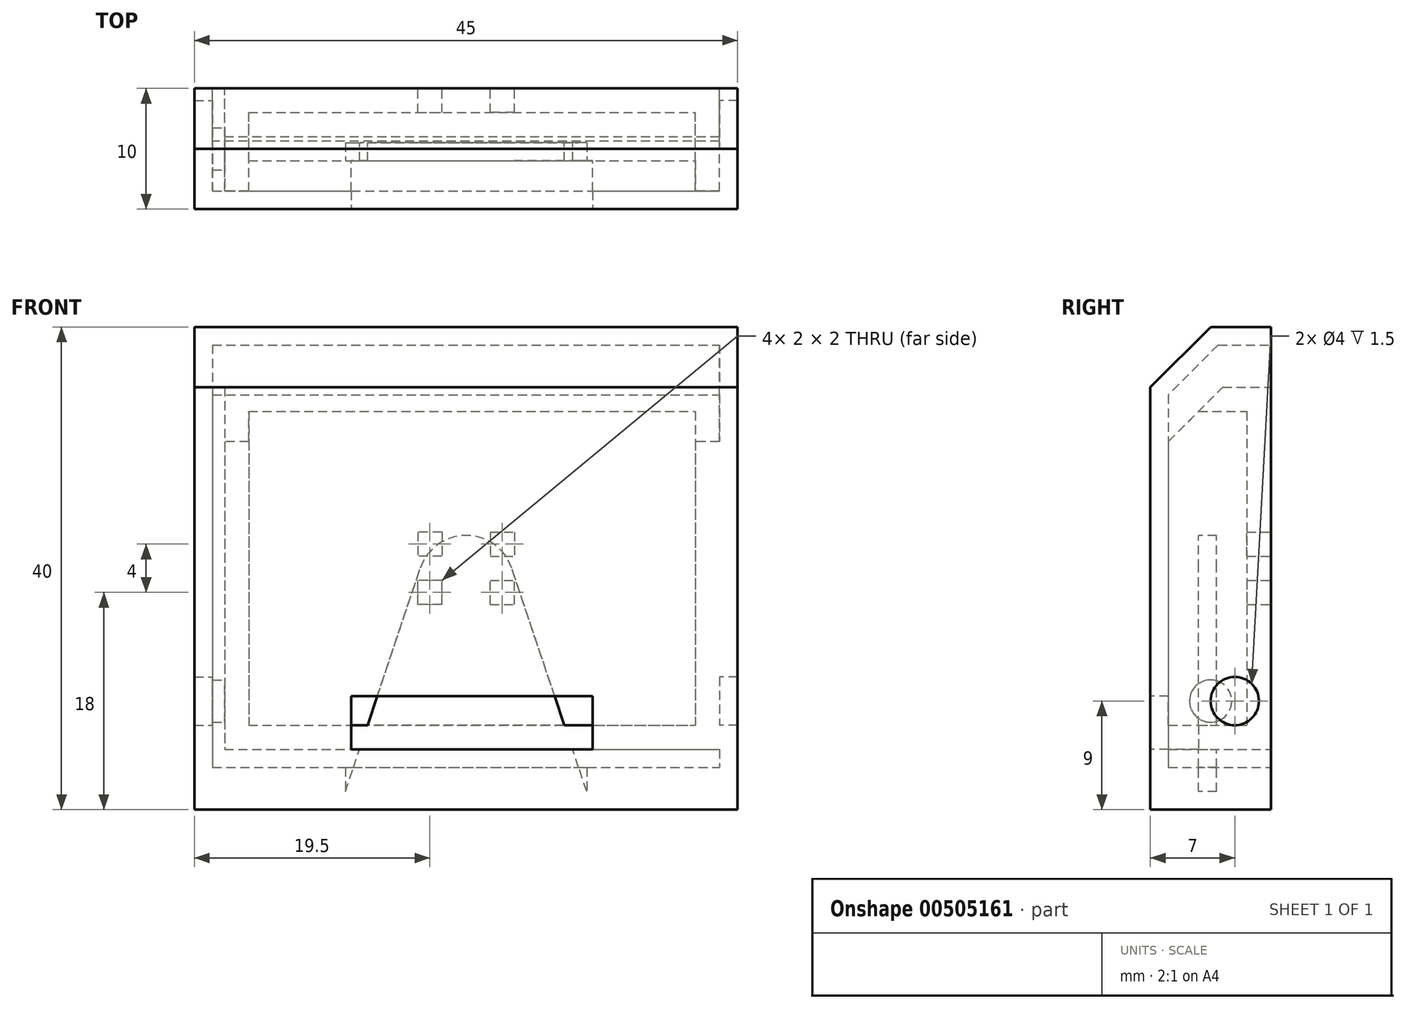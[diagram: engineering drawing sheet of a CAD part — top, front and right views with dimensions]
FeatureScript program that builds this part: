
annotation { "Feature Type Name" : "Feature", "Feature Type Description" : "" }
export const myFeature = defineFeature(function(context is Context, id is Id, definition is map)
    precondition{}
    {
        {
            var Q0;
            Q0=qCreatedBy(makeId("Front.planeOp"),FACE);
            var sketch = newSketch(context, id + "F0", { "sketchPlane" : qUnion([Q0])});
            skLineSegment(sketch, "E0.bottom", {"start": v(-20, 15) * mm, "end": v(21, 15) * mm});
            skLineSegment(sketch, "E0.top", {"start": v(-20, -15) * mm, "end": v(21, -15) * mm});
            skLineSegment(sketch, "E0.left", {"start": v(-20, 15) * mm, "end": v(-20, -15) * mm});
            skLineSegment(sketch, "E0.right", {"start": v(21, 15) * mm, "end": v(21, -15) * mm});
            skSolve(sketch);
        }
        {
            var Q0;
            Q0=makeQuery(id+"F0.imprint","IMPRINT",FACE,{"disambiguationData":[TD([[makeQuery(id+"F0.imprint","IMPRINT",EDGE,{"derivedFrom":sQuery(id+"F0.wireOp",EDGE,"E0.bottom")}),-1.0]])]});
            extrude(context, id + "F1", {"entities" : qUnion([Q0]), "depth" : 9 * mm, "offsetDistance" : 25 * mm});
        }
        {
            var Q0;
            Q0=makeQuery(id+"F1.opExtrude","CAP_FACE",FACE,{"disambiguationData":[OSD([sQuery(id+"F0.wireOp",EDGE,"E0.bottom"),sQuery(id+"F0.wireOp",EDGE,"E0.top"),sQuery(id+"F0.wireOp",EDGE,"E0.left"),sQuery(id+"F0.wireOp",EDGE,"E0.right"),sQuery(id+"F0.wireOp",EDGE,"RBEQEyJk-aGxJ-4fvi-WYVx-bpJPuigMuznj.bottom"),sQuery(id+"F0.wireOp",EDGE,"RBEQEyJk-aGxJ-4fvi-WYVx-bpJPuigMuznj.top"),sQuery(id+"F0.wireOp",EDGE,"RBEQEyJk-aGxJ-4fvi-WYVx-bpJPuigMuznj.left"),sQuery(id+"F0.wireOp",EDGE,"RBEQEyJk-aGxJ-4fvi-WYVx-bpJPuigMuznj.right"),sQuery(id+"F0.wireOp",EDGE,"3556d0db-5f9f-403e-93f9-4f2c554f31b60.MirrorCS"),sQuery(id+"F0.wireOp",EDGE,"3556d0db-5f9f-403e-93f9-4f2c554f31b61.MirrorCS"),sQuery(id+"F0.wireOp",EDGE,"3556d0db-5f9f-403e-93f9-4f2c554f31b62.MirrorCS"),sQuery(id+"F0.wireOp",EDGE,"3556d0db-5f9f-403e-93f9-4f2c554f31b63.MirrorCS"),sQuery(id+"F0.wireOp",EDGE,"c14dda6f-b8be-4261-b637-7746e7f6adf01.MirrorCS"),sQuery(id+"F0.wireOp",EDGE,"c14dda6f-b8be-4261-b637-7746e7f6adf02.MirrorCS"),sQuery(id+"F0.wireOp",EDGE,"c14dda6f-b8be-4261-b637-7746e7f6adf04.MirrorCS"),sQuery(id+"F0.wireOp",EDGE,"c14dda6f-b8be-4261-b637-7746e7f6adf05.MirrorCS"),sQuery(id+"F0.wireOp",EDGE,"c14dda6f-b8be-4261-b637-7746e7f6adf06.MirrorCS"),sQuery(id+"F0.wireOp",EDGE,"c14dda6f-b8be-4261-b637-7746e7f6adf08.MirrorCS"),sQuery(id+"F0.wireOp",EDGE,"c14dda6f-b8be-4261-b637-7746e7f6adf09.MirrorCS"),sQuery(id+"F0.wireOp",EDGE,"c14dda6f-b8be-4261-b637-7746e7f6adf012.MirrorCS")])],"isStart":false});
            shell(context, id + "F2", {"entities" : qUnion([Q0]), "thickness" : 2 * mm});
        }
        {
            var Q0;
            Q0=makeQuery(id+"F0.imprint","IMPRINT",FACE,{"disambiguationData":[TD([[makeQuery(id+"F0.imprint","IMPRINT",EDGE,{"derivedFrom":sQuery(id+"F0.wireOp",EDGE,"E0.bottom")}),-1.0]])]});
            var sketch = newSketch(context, id + "F3", { "sketchPlane" : qUnion([Q0])});
            skLineSegment(sketch, "E1.bottom", {"start": v(-3, -2) * mm, "end": v(3, -2) * mm, "construction": true});
            skLineSegment(sketch, "E1.top", {"start": v(-3, 2) * mm, "end": v(3, 2) * mm, "construction": true});
            skLineSegment(sketch, "E1.left", {"start": v(-3, -2) * mm, "end": v(-3, 2) * mm, "construction": true});
            skLineSegment(sketch, "E1.right", {"start": v(3, -2) * mm, "end": v(3, 2) * mm, "construction": true});
            skPoint(sketch, "E1.middle", {"position": v(0, 0) * mm});
            skLineSegment(sketch, "E2.bottom", {"start": v(-2, -3) * mm, "end": v(-4, -3) * mm});
            skLineSegment(sketch, "E2.top", {"start": v(-2, -1) * mm, "end": v(-4, -1) * mm});
            skLineSegment(sketch, "E2.left", {"start": v(-2, -3) * mm, "end": v(-2, -1) * mm});
            skLineSegment(sketch, "E2.right", {"start": v(-4, -3) * mm, "end": v(-4, -1) * mm});
            skPoint(sketch, "E2.middle", {"position": v(-3, -2) * mm});
            skLineSegment(sketch, "E3.MirrorCS", {"start": v(4, -3) * mm, "end": v(4, -1) * mm});
            skLineSegment(sketch, "E4.MirrorCS", {"start": v(2, -1) * mm, "end": v(4, -1) * mm});
            skLineSegment(sketch, "E5.MirrorCS", {"start": v(2, -3) * mm, "end": v(2, -1) * mm});
            skLineSegment(sketch, "E6.MirrorCS", {"start": v(2, -3) * mm, "end": v(4, -3) * mm});
            skPoint(sketch, "E7.MirrorP", {"position": v(3, -2) * mm});
            skLineSegment(sketch, "E8.MirrorCS", {"start": v(2, 3) * mm, "end": v(2, 1) * mm});
            skLineSegment(sketch, "E9.MirrorCS", {"start": v(2, 1) * mm, "end": v(4, 1) * mm});
            skPoint(sketch, "E10.MirrorP", {"position": v(-3, 2) * mm});
            skLineSegment(sketch, "E11.MirrorCS", {"start": v(-4, 3) * mm, "end": v(-4, 1) * mm});
            skLineSegment(sketch, "E12.MirrorCS", {"start": v(4, 3) * mm, "end": v(4, 1) * mm});
            skLineSegment(sketch, "E13.MirrorCS", {"start": v(2, 3) * mm, "end": v(4, 3) * mm});
            skLineSegment(sketch, "E14.MirrorCS", {"start": v(-2, 3) * mm, "end": v(-2, 1) * mm});
            skLineSegment(sketch, "E15.MirrorCS", {"start": v(-2, 1) * mm, "end": v(-4, 1) * mm});
            skPoint(sketch, "E16.MirrorP", {"position": v(3, 2) * mm});
            skLineSegment(sketch, "E17.MirrorCS", {"start": v(-2, 3) * mm, "end": v(-4, 3) * mm});
            skSolve(sketch);
        }
        {
            var Q0;
            Q0 = qSketchRegion(id + "F3", true);
            extrude(context, id + "F4", {"entities" : qUnion([Q0]), "operationType" : NewBodyOperationType.REMOVE, "depth" : 4 * mm});
        }
        {
            var Q0;
            Q0=makeQuery(id+"F1.opExtrude","SWEPT_FACE",FACE,{"disambiguationData":[OSD([sQuery(id+"F0.wireOp",EDGE,"E0.right")])]});
            var sketch = newSketch(context, id + "F5", { "sketchPlane" : qUnion([Q0])});
            skCircle(sketch, "E18", {"center": v(-5, -11) * mm, "radius": 1.75 * mm});
            skSolve(sketch);
        }
        {
            var Q0;
            Q0 = qSketchRegion(id + "F5", true);
            extrude(context, id + "F6", {"entities" : qUnion([Q0]), "operationType" : NewBodyOperationType.ADD, "depth" : 1 * mm, "offsetDistance" : 25 * mm});
        }
        {
            var Q0;
            Q0=makeQuery(id+"F1.opExtrude","SWEPT_FACE",FACE,{"disambiguationData":[OSD([sQuery(id+"F0.wireOp",EDGE,"E0.left")])]});
            var sketch = newSketch(context, id + "F7", { "sketchPlane" : qUnion([Q0])});
            skCircle(sketch, "E19", {"center": v(5, -11) * mm, "radius": 1.75 * mm});
            skSolve(sketch);
        }
        {
            var Q0;
            Q0 = qSketchRegion(id + "F7", true);
            extrude(context, id + "F8", {"entities" : qUnion([Q0]), "operationType" : NewBodyOperationType.ADD, "depth" : 1 * mm, "offsetDistance" : 25 * mm});
        }
        {
            var Q0;
            Q0=qCreatedBy(makeId("Front.planeOp"),FACE);
            var sketch = newSketch(context, id + "F9", { "sketchPlane" : qUnion([Q0])});
            skLineSegment(sketch, "E20.bottom", {"start": v(-22.5, 20) * mm, "end": v(22.5, 20) * mm});
            skLineSegment(sketch, "E20.top", {"start": v(-22.5, -20) * mm, "end": v(22.5, -20) * mm});
            skLineSegment(sketch, "E20.left", {"start": v(-22.5, 20) * mm, "end": v(-22.5, -20) * mm});
            skLineSegment(sketch, "E20.right", {"start": v(22.5, 20) * mm, "end": v(22.5, -20) * mm});
            skPoint(sketch, "E20.middle", {"position": v(0, 0) * mm});
            skSolve(sketch);
        }
        {
            var Q0;
            Q0=makeQuery(id+"F9.imprint","IMPRINT",FACE,{"disambiguationData":[TD([[makeQuery(id+"F9.imprint","IMPRINT",EDGE,{"derivedFrom":sQuery(id+"F9.wireOp",EDGE,"E20.bottom")}),-1.0]])]});
            extrude(context, id + "F10", {"entities" : qUnion([Q0]), "depth" : 10 * mm});
        }
        {
            var Q0;
            Q0=makeQuery(id+"F10.opExtrude","CAP_EDGE",EDGE,{"disambiguationData":[OSD([sQuery(id+"F9.wireOp",EDGE,"E20.bottom")])],"isStart":false});
            chamfer(context, id + "F11", {"entities" : qUnion([Q0]), "width" : 5 * mm, "tangentPropagation" : true});
        }
        {
            var Q0;
            Q0=makeQuery(id+"F10.opExtrude","CAP_FACE",FACE,{"disambiguationData":[OSD([sQuery(id+"F9.wireOp",EDGE,"E20.bottom"),sQuery(id+"F9.wireOp",EDGE,"E20.top"),sQuery(id+"F9.wireOp",EDGE,"E20.left"),sQuery(id+"F9.wireOp",EDGE,"E20.right")])],"isStart":true});
            shell(context, id + "F12", {"entities" : qUnion([Q0]), "thickness" : 1.5 * mm});
        }
        {
            var Q0;
            Q0=makeQuery(id+"F1.opExtrude","CAP_EDGE",EDGE,{"disambiguationData":[OSD([sQuery(id+"F0.wireOp",EDGE,"E0.bottom")])],"isStart":false});
            chamfer(context, id + "F13", {"entities" : qUnion([Q0]), "width" : 5 * mm, "tangentPropagation" : true});
        }
        {
            var Q0;
            Q0=makeQuery(id+"F1.opExtrude","SWEPT_FACE",FACE,{"disambiguationData":[OSD([sQuery(id+"F0.wireOp",EDGE,"E0.top")])]});
            var sketch = newSketch(context, id + "F14", { "sketchPlane" : qUnion([Q0])});
            skLineSegment(sketch, "E21.bottom", {"start": v(-9.5, 6) * mm, "end": v(10.5, 6) * mm});
            skLineSegment(sketch, "E21.top", {"start": v(-9.5, 12) * mm, "end": v(10.5, 12) * mm});
            skLineSegment(sketch, "E21.left", {"start": v(-9.5, 6) * mm, "end": v(-9.5, 12) * mm});
            skLineSegment(sketch, "E21.right", {"start": v(10.5, 6) * mm, "end": v(10.5, 12) * mm});
            skPoint(sketch, "E21.middle", {"position": v(0.5, 9) * mm});
            skSolve(sketch);
        }
        {
            var Q0;
            Q0 = qSketchRegion(id + "F14", true);
            extrude(context, id + "F15", {"entities" : qUnion([Q0]), "operationType" : NewBodyOperationType.REMOVE, "oppositeDirection" : true, "depth" : 4.4 * mm});
        }
        {
            var Q0;
            Q0=makeQuery(id+"F12.opShell","OFFSET_FACE",FACE,{"disambiguationData":[OSD([sQuery(id+"F9.wireOp",EDGE,"E20.bottom"),sQuery(id+"F9.wireOp",EDGE,"E20.top"),sQuery(id+"F9.wireOp",EDGE,"E20.left"),sQuery(id+"F9.wireOp",EDGE,"E20.right")])]});
            cPlane(context, id + "F16", {"entities" : qUnion([Q0]), "cplaneType" : CPlaneType.OFFSET, "offset" : 2.5 * mm, "width" : 150 * mm, "height" : 150 * mm});
        }
        {
            var Q0;
            Q0=qCreatedBy(id+"F16.planeOp",FACE);
            var sketch = newSketch(context, id + "F17", { "sketchPlane" : qUnion([Q0])});
            skLineSegment(sketch, "E22", {"start": v(21, -18.5) * mm, "end": v(-21, -18.5) * mm});
            skLineSegment(sketch, "E23", {"start": v(-10, -18.5) * mm, "end": v(-3.8, 0) * mm});
            skLineSegment(sketch, "E24.MirrorCS", {"start": v(10, -18.5) * mm, "end": v(3.8, 0) * mm});
            skArc(sketch, "E25", {"start": v(3.8, 0) * mm, "mid": v(0, 2.73) * mm, "end": v(-3.8, 0) * mm});
            skSolve(sketch);
        }
        {
            var Q0;
            {var subQ0=sQuery(id+"F17.wireOp",EDGE,"E23");Q0=makeQuery(id+"F17.imprint","IMPRINT",FACE,{"disambiguationData":[TD([[makeQuery(id+"F17.imprint","IMPRINT",EDGE,{"derivedFrom":subQ0}),-1.0]])]});}
            extrude(context, id + "F18", {"entities" : qUnion([Q0]), "operationType" : NewBodyOperationType.ADD, "depth" : 1.5 * mm});
        }
        {
            var Q0;
            Q0=makeQuery(id+"F12.opShell","OFFSET_FACE",FACE,{"disambiguationData":[OSD([sQuery(id+"F9.wireOp",EDGE,"E20.left")])]});
            var sketch = newSketch(context, id + "F19", { "sketchPlane" : qUnion([Q0])});
            skCircle(sketch, "E26", {"center": v(-3, -11) * mm, "radius": 2 * mm});
            skSolve(sketch);
        }
        {
            var Q0;
            Q0=makeQuery(id+"F19.imprint","IMPRINT",FACE,{"disambiguationData":[TD([[makeQuery(id+"F19.imprint","IMPRINT",EDGE,{"derivedFrom":sQuery(id+"F19.wireOp",EDGE,"E26")}),1.0]])]});
            extrude(context, id + "F20", {"entities" : qUnion([Q0]), "operationType" : NewBodyOperationType.REMOVE, "oppositeDirection" : true, "depth" : 25 * mm});
        }
        {
            var Q0;
            Q0=makeQuery(id+"F12.opShell","OFFSET_FACE",FACE,{"disambiguationData":[OSD([sQuery(id+"F9.wireOp",EDGE,"E20.right")])]});
            var sketch = newSketch(context, id + "F21", { "sketchPlane" : qUnion([Q0])});
            skCircle(sketch, "E27", {"center": v(3, -11) * mm, "radius": 2 * mm});
            skSolve(sketch);
        }
        {
            var Q0;
            Q0=makeQuery(id+"F21.imprint","IMPRINT",FACE,{"disambiguationData":[TD([[makeQuery(id+"F21.imprint","IMPRINT",EDGE,{"derivedFrom":sQuery(id+"F21.wireOp",EDGE,"E27")}),1.0]])]});
            extrude(context, id + "F22", {"entities" : qUnion([Q0]), "operationType" : NewBodyOperationType.REMOVE, "oppositeDirection" : true, "depth" : 25 * mm});
        }
        {
            var Q0;
            Q0=makeQuery(id+"F12.opShell","OFFSET_FACE",FACE,{"disambiguationData":[OSD([sQuery(id+"F9.wireOp",EDGE,"E20.top")])]});
            extrude(context, id + "F23", {"entities" : qUnion([Q0]), "operationType" : NewBodyOperationType.ADD, "depth" : 2 * mm, "offsetDistance" : 25 * mm});
        }
    });
